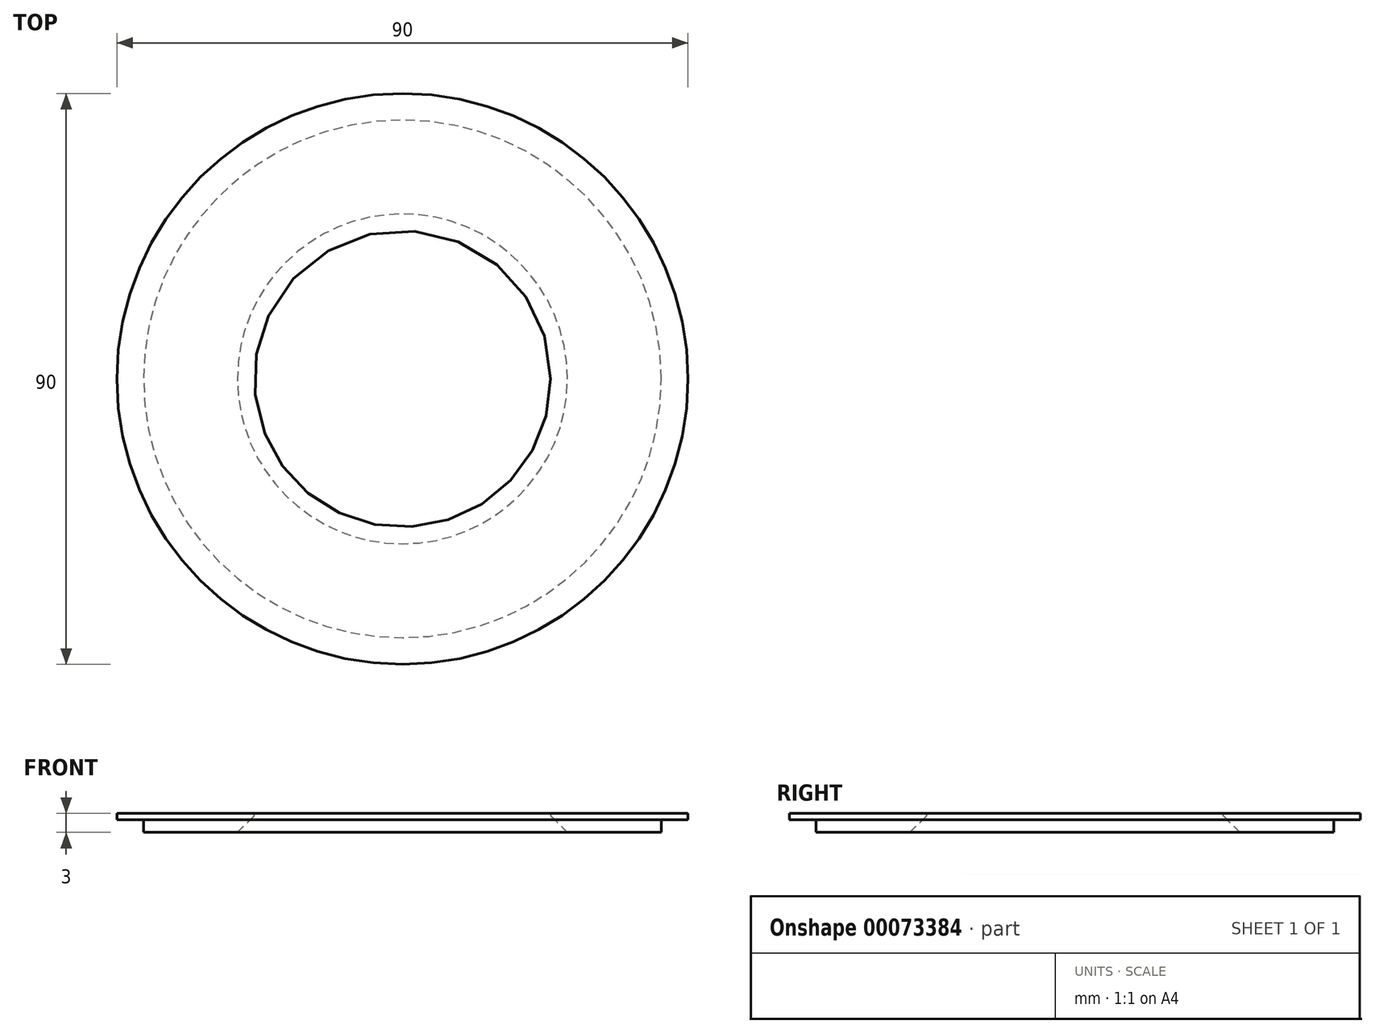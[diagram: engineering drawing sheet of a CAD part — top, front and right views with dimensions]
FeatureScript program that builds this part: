
annotation { "Feature Type Name" : "Feature", "Feature Type Description" : "" }
export const myFeature = defineFeature(function(context is Context, id is Id, definition is map)
    precondition{}
    {
        {
            var Q0;
            Q0=qCreatedBy(makeId("Front.planeOp"),FACE);
            var sketch = newSketch(context, id + "F0", { "sketchPlane" : qUnion([Q0])});
            skLineSegment(sketch, "E0", {"start": v(0.43, -0.43) * mm, "end": v(3, -3) * mm});
            skLineSegment(sketch, "E1", {"start": v(3, -3) * mm, "end": v(17.8, -3) * mm});
            skLineSegment(sketch, "E2", {"start": v(17.8, -3) * mm, "end": v(17.8, -1) * mm});
            skLineSegment(sketch, "E3", {"start": v(17.8, -1) * mm, "end": v(22, -1) * mm});
            skLineSegment(sketch, "E4", {"start": v(22, -1) * mm, "end": v(22, 0) * mm});
            skLineSegment(sketch, "E5", {"start": v(22, 0) * mm, "end": v(0.6, 0) * mm});
            skLineSegment(sketch, "E6", {"start": v(-23, 50.02) * mm, "end": v(-23, -56.54) * mm, "construction": true});
            skPoint(sketch, "E7.visualSharp", {"position": v(0, 0) * mm});
            skArc(sketch, "E7.filletArc", {"start": v(0.6, 0) * mm, "mid": v(0.37, -0.15) * mm, "end": v(0.43, -0.43) * mm});
            skSolve(sketch);
        }
        {
            var Q0;
            Q0=makeQuery(id+"F0.imprint","IMPRINT",FACE,{"disambiguationData":[TD([[makeQuery(id+"F0.imprint","IMPRINT",EDGE,{"derivedFrom":sQuery(id+"F0.wireOp",EDGE,"E0")}),1.0]])]});
            var Q1;
            Q1=sQuery(id+"F0.wireOp",EDGE,"E6");
            revolve(context, id + "F1", {"entities" : qUnion([Q0]), "axis" : qUnion([Q1]), "revolveType" : RevolveType.FULL});
        }
    });
